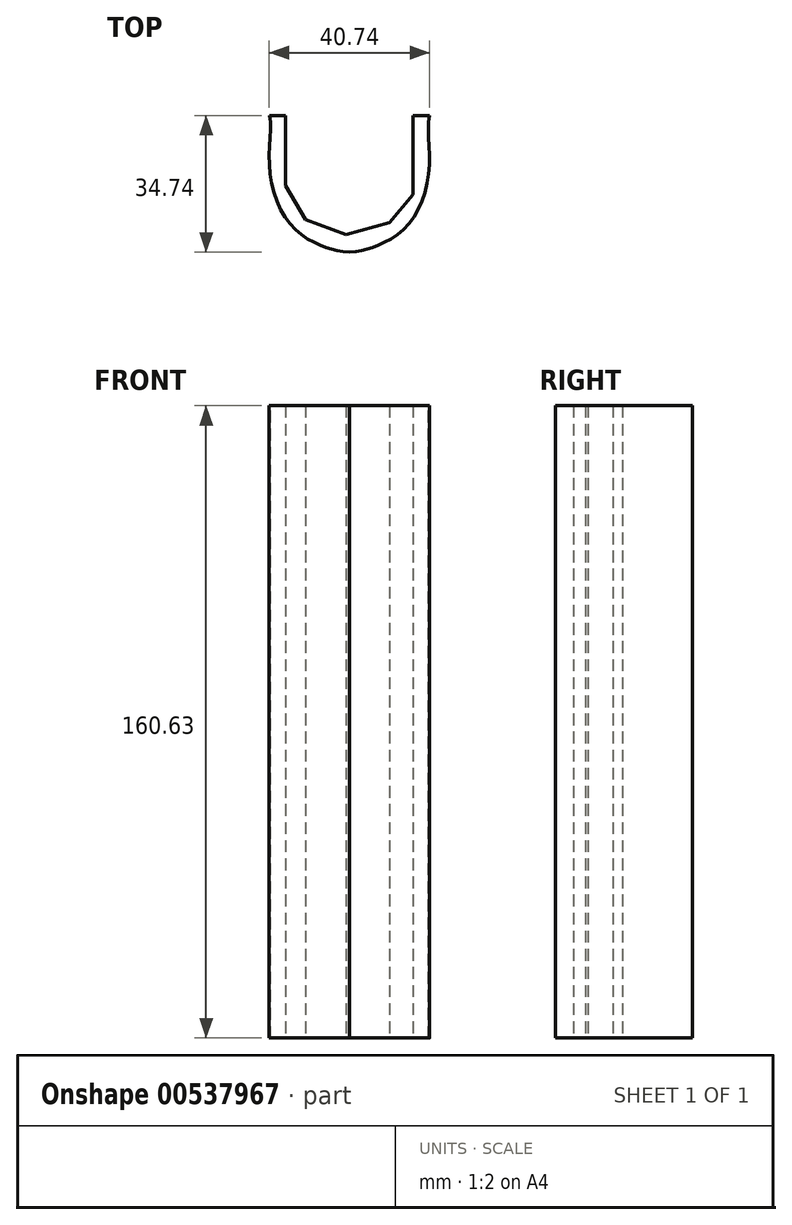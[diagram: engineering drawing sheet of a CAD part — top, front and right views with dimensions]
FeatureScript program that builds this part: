
annotation { "Feature Type Name" : "Feature", "Feature Type Description" : "" }
export const myFeature = defineFeature(function(context is Context, id is Id, definition is map)
    precondition{}
    {
        {
            var Q0;
            Q0=qCreatedBy(makeId("Top.planeOp"),FACE);
            var sketch = newSketch(context, id + "F0", { "sketchPlane" : qUnion([Q0])});
            skFitSpline(sketch, "E0", {"points": [v(0, 0) * mm, v(0, -12.9) * mm, v(-5.16, -27.46) * mm, v(-13.65, -33.22) * mm, v(-20.32, -34.74) * mm], "startDerivative": vector(-8.04, -35.25) * mm, "endDerivative": vector(-39.51, -4.22) * mm});
            skFitSpline(sketch, "E1.MirrorCS", {"points": [v(-40.64, 0) * mm, v(-40.64, -12.9) * mm, v(-35.48, -27.46) * mm, v(-26.98, -33.22) * mm, v(-20.32, -34.74) * mm], "startDerivative": vector(8.04, -35.25) * mm, "endDerivative": vector(39.51, -4.22) * mm});
            skLineSegment(sketch, "E2", {"start": v(-40.64, 0) * mm, "end": v(-36.49, 0) * mm});
            skLineSegment(sketch, "E3", {"start": v(-36.49, 0) * mm, "end": v(-36.49, -17.78) * mm});
            skLineSegment(sketch, "E4", {"start": v(-36.49, -17.78) * mm, "end": v(-31.44, -26.44) * mm});
            skLineSegment(sketch, "E5", {"start": v(-31.44, -26.44) * mm, "end": v(-21.15, -30.22) * mm});
            skLineSegment(sketch, "E6", {"start": v(-21.15, -30.22) * mm, "end": v(-10.15, -27.16) * mm});
            skLineSegment(sketch, "E7", {"start": v(-10.15, -27.16) * mm, "end": v(-4.2, -20.12) * mm});
            skLineSegment(sketch, "E8", {"start": v(-4.2, -20.12) * mm, "end": v(-4.2, 0) * mm});
            skLineSegment(sketch, "E9", {"start": v(-4.2, 0) * mm, "end": v(0, 0) * mm});
            skSolve(sketch);
        }
        {
            var Q0;
            Q0=qCreatedBy(makeId("Front.planeOp"),FACE);
            var sketch = newSketch(context, id + "F1", { "sketchPlane" : qUnion([Q0])});
            skLineSegment(sketch, "E10", {"start": v(-20.37, 0) * mm, "end": v(-20.37, -160.63) * mm});
            skSolve(sketch);
        }
        {
            var Q0;
            Q0=makeQuery(id+"F0.imprint","IMPRINT",FACE,{"disambiguationData":[TD([[makeQuery(id+"F0.imprint","IMPRINT",EDGE,{"derivedFrom":sQuery(id+"F0.wireOp",EDGE,"E0")}),-1.0]])]});
            var Q1;
            Q1=sQuery(id+"F1.wireOp",EDGE,"E10");
            sweep(context, id + "F2", {"profiles" : qUnion([Q0]), "path" : qUnion([Q1])});
        }
    });
